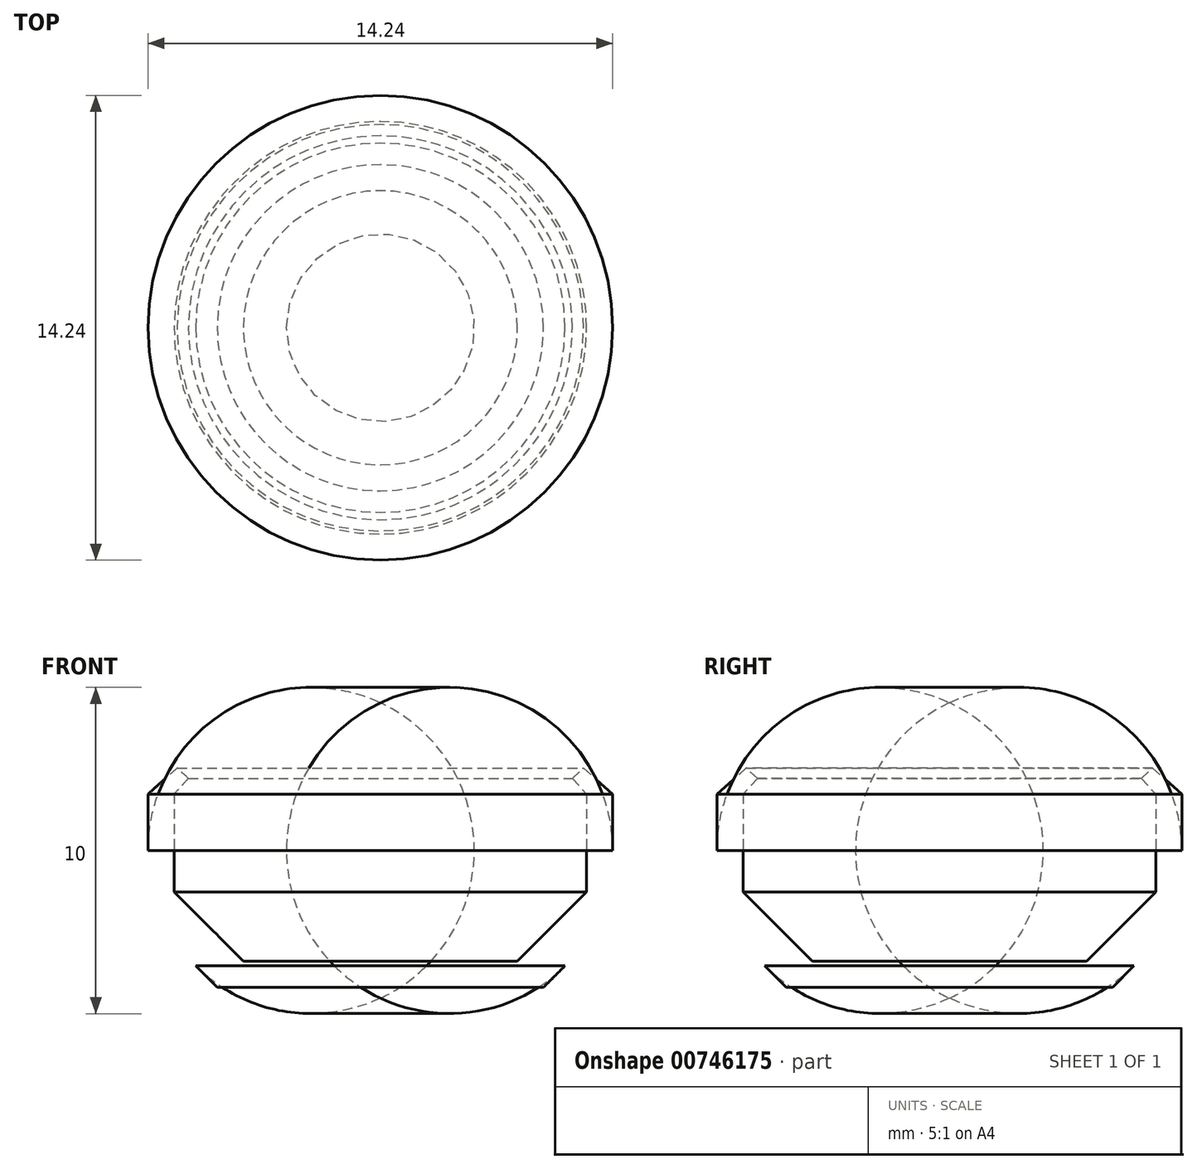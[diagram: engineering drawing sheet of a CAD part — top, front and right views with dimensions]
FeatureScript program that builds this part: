
annotation { "Feature Type Name" : "Feature", "Feature Type Description" : "" }
export const myFeature = defineFeature(function(context is Context, id is Id, definition is map)
    precondition{}
    {
        {
            var Q0;
            Q0=qCreatedBy(makeId("Top.planeOp"),FACE);
            var sketch = newSketch(context, id + "F0", { "sketchPlane" : qUnion([Q0])});
            skCircle(sketch, "E0", {"center": v(0, 0) * mm, "radius": 5 * mm});
            skSolve(sketch);
        }
        {
            var Q0;
            Q0=makeQuery(id+"F0.imprint","IMPRINT",FACE,{"disambiguationData":[TD([[makeQuery(id+"F0.imprint","IMPRINT",EDGE,{"derivedFrom":sQuery(id+"F0.wireOp",EDGE,"E0")}),1.0]])]});
            extrude(context, id + "F1", {"entities" : qUnion([Q0]), "depth" : 0.8 * mm, "offsetDistance" : 25 * mm, "hasDraft" : true, "draftAngle" : 45 * degree, "draftPullDirection" : true});
        }
        {
            var Q0;
            Q0=qCreatedBy(makeId("Right.planeOp"),FACE);
            var sketch = newSketch(context, id + "F2", { "sketchPlane" : qUnion([Q0])});
            skLineSegment(sketch, "E1", {"start": v(-5, 0) * mm, "end": v(-7.12, 2.12) * mm});
            skLineSegment(sketch, "E2", {"start": v(-6.32, 2.92) * mm, "end": v(-4.2, 0.8) * mm});
            skLineSegment(sketch, "E3", {"start": v(-4.2, 0.8) * mm, "end": v(-5, 0) * mm});
            skLineSegment(sketch, "E4", {"start": v(-7.12, 2.12) * mm, "end": v(-7.12, 5.92) * mm});
            skLineSegment(sketch, "E5", {"start": v(-6.32, 2.92) * mm, "end": v(-6.32, 5.92) * mm});
            skLineSegment(sketch, "E6", {"start": v(-6.32, 5.92) * mm, "end": v(-5.88, 6.4) * mm});
            skLineSegment(sketch, "E7", {"start": v(-5.88, 6.4) * mm, "end": v(-6.23, 6.72) * mm});
            skLineSegment(sketch, "E8", {"start": v(-6.23, 6.72) * mm, "end": v(-7.12, 5.92) * mm});
            skSolve(sketch);
        }
        {
            var Q0;
            Q0=makeQuery(id+"F2.imprint","IMPRINT",FACE,{"disambiguationData":[TD([[makeQuery(id+"F2.imprint","IMPRINT",EDGE,{"derivedFrom":sQuery(id+"F2.wireOp",EDGE,"E1")}),-1.0]])]});
            var Q1;
            Q1=makeQuery(id+"F1.opExtrude","CAP_EDGE",EDGE,{"disambiguationData":[OSD([sQuery(id+"F0.wireOp",EDGE,"E0")])],"isStart":false});
            revolve(context, id + "F3", {"operationType" : NewBodyOperationType.ADD, "surfaceOperationType" : NewSurfaceOperationType.NEW, "entities" : qUnion([Q0]), "axis" : qUnion([Q1]), "revolveType" : RevolveType.FULL});
        }
        {
            var Q0;
            Q0=makeQuery(id+"F3.opRevolve","SWEPT_EDGE",EDGE,{"disambiguationData":[OSD([sQuery(id+"F2.wireOp",EDGE,"E1"),sQuery(id+"F2.wireOp",EDGE,"E4")])]});
            fillet(context, id + "F4", {"entities" : qUnion([Q0]), "radius" : 5 * mm, "tangentPropagation" : true, "allowEdgeOverflow" : false});
        }
    });
